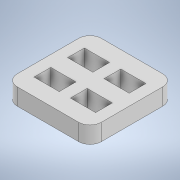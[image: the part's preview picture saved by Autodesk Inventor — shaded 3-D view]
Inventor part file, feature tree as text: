
AUTODESK INVENTOR PART (.ipt)
format: ipt  version: 2020 (Build 240168000, 168)  size: 125,440 bytes
history: native  units: in
note: dims shown in document units (in); Inventor stores cm internally (conversion verified against a paired STEP export)
features: extrude x1, sketch x1
ambient origin geometry x8: Origin, YZ Plane, XZ Plane, XY Plane, X Axis, Y Axis, Z Axis, Center Point
bodies: Solid1 (feature_tree)
feature tree (2):
  extrude  "Extrusion1"  Depth=0.4331in
  sketch  "Sketch1"  dims[d0=0.0787in d1=0.4331in d2=0.4331in d5=0.1181in d6=0.1772in d7=0.0787in d8=0.1181in d11=0.1181in d12=0.0in]
